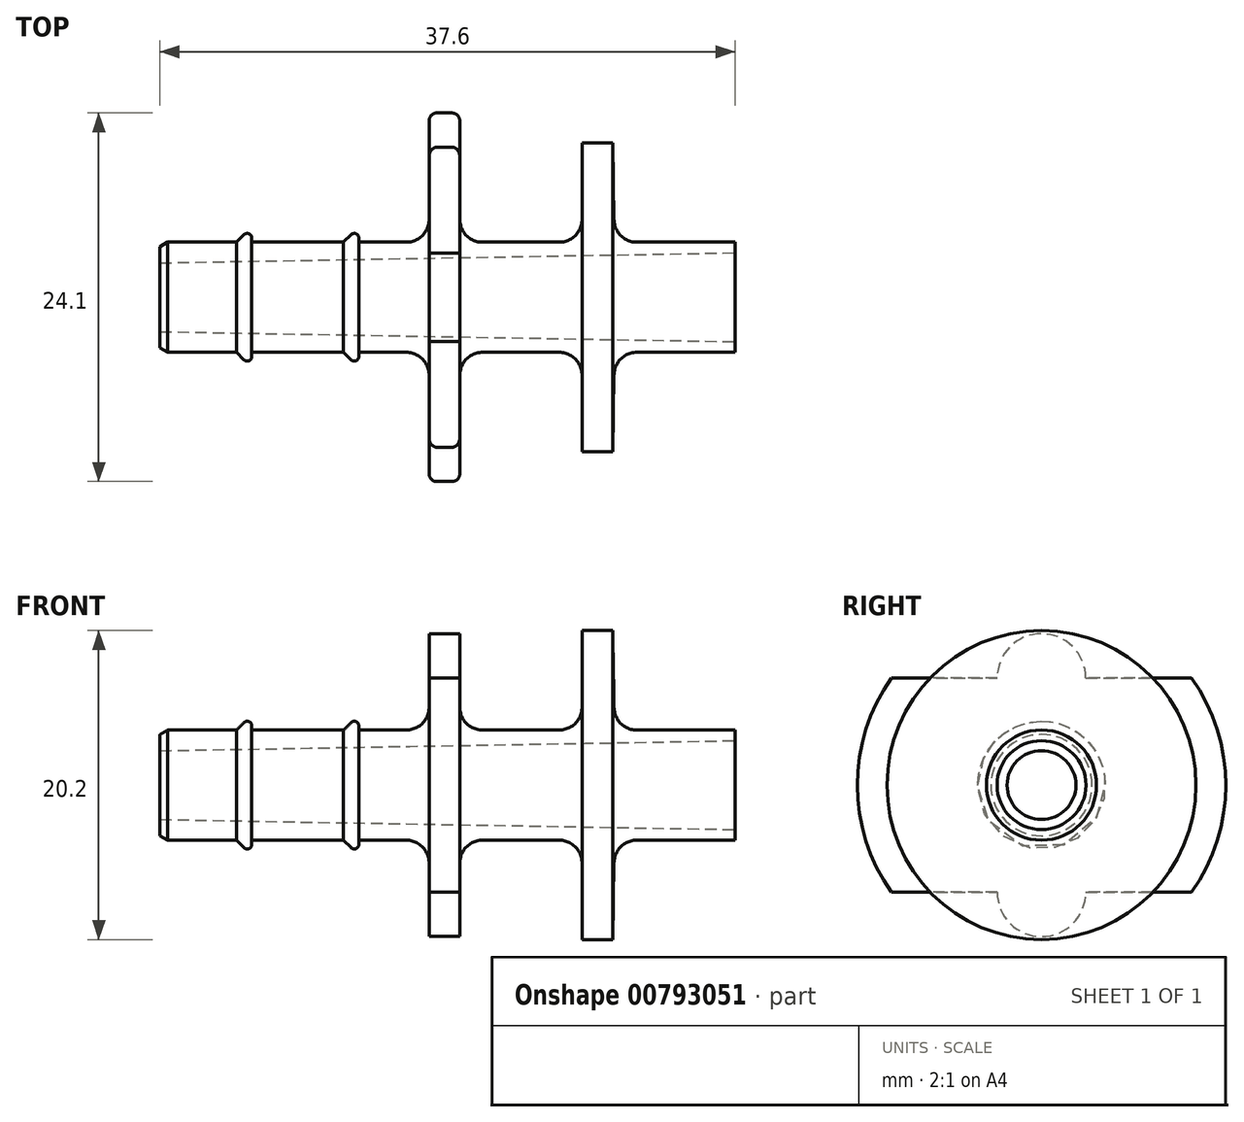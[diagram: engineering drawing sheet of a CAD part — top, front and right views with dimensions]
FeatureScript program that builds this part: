
annotation { "Feature Type Name" : "Feature", "Feature Type Description" : "" }
export const myFeature = defineFeature(function(context is Context, id is Id, definition is map)
    precondition{}
    {
        {
            var Q0;
            Q0=qCreatedBy(makeId("Front.planeOp"),FACE);
            var sketch = newSketch(context, id + "F0", { "sketchPlane" : qUnion([Q0])});
            skLineSegment(sketch, "E0", {"start": v(-19.78, 2.25) * mm, "end": v(17.82, 2.9) * mm});
            skLineSegment(sketch, "E1", {"start": v(17.82, 3.6) * mm, "end": v(11.4, 3.6) * mm});
            skLineSegment(sketch, "E2", {"start": v(17.82, 3.6) * mm, "end": v(17.82, 2.9) * mm});
            skLineSegment(sketch, "E3", {"start": v(-19.78, 3.6) * mm, "end": v(-19.78, 2.25) * mm});
            skLineSegment(sketch, "E4", {"start": v(9.9, 5.07) * mm, "end": v(9.82, 10.1) * mm});
            skLineSegment(sketch, "E5", {"start": v(9.82, 10.1) * mm, "end": v(7.82, 10.1) * mm});
            skLineSegment(sketch, "E6", {"start": v(7.82, 10.1) * mm, "end": v(7.82, 5.1) * mm});
            skLineSegment(sketch, "E7", {"start": v(-0.18, 5.1) * mm, "end": v(-0.18, 11.55) * mm});
            skLineSegment(sketch, "E8", {"start": v(-0.68, 12.05) * mm, "end": v(-1.68, 12.05) * mm});
            skLineSegment(sketch, "E9", {"start": v(-2.18, 11.55) * mm, "end": v(-2.18, 5.1) * mm});
            skLineSegment(sketch, "E10", {"start": v(-9.19, 0) * mm, "end": v(9.2, 0) * mm, "construction": true});
            skPoint(sketch, "E11.visualSharp", {"position": v(-2.18, 12.05) * mm});
            skArc(sketch, "E11.filletArc", {"start": v(-1.68, 12.05) * mm, "mid": v(-2.03, 11.9) * mm, "end": v(-2.18, 11.55) * mm});
            skPoint(sketch, "E12.visualSharp", {"position": v(-0.18, 12.05) * mm});
            skArc(sketch, "E12.filletArc", {"start": v(-0.18, 11.55) * mm, "mid": v(-0.32, 11.9) * mm, "end": v(-0.68, 12.05) * mm});
            skPoint(sketch, "E13.newPointB", {"position": v(-5.55, 3.6) * mm});
            skArc(sketch, "E13.filletArc", {"start": v(9.9, 5.07) * mm, "mid": v(10.36, 4.03) * mm, "end": v(11.4, 3.6) * mm});
            skLineSegment(sketch, "E14", {"start": v(11.4, 3.6) * mm, "end": v(7.82, 3.6) * mm});
            skLineSegment(sketch, "E15", {"start": v(-0.18, 3.6) * mm, "end": v(-2.18, 3.6) * mm});
            skLineSegment(sketch, "E16", {"start": v(1.32, 3.6) * mm, "end": v(6.32, 3.6) * mm});
            skLineSegment(sketch, "E17", {"start": v(-3.68, 3.6) * mm, "end": v(-19.78, 3.6) * mm});
            skPoint(sketch, "E18.visualSharp", {"position": v(7.82, 3.6) * mm});
            skArc(sketch, "E18.filletArc", {"start": v(6.32, 3.6) * mm, "mid": v(7.38, 4.04) * mm, "end": v(7.82, 5.1) * mm});
            skPoint(sketch, "E19.visualSharp", {"position": v(-0.18, 3.6) * mm});
            skArc(sketch, "E19.filletArc", {"start": v(-0.18, 5.1) * mm, "mid": v(0.26, 4.04) * mm, "end": v(1.32, 3.6) * mm});
            skPoint(sketch, "E20.visualSharp", {"position": v(-2.18, 3.6) * mm});
            skArc(sketch, "E20.filletArc", {"start": v(-3.68, 3.6) * mm, "mid": v(-2.62, 4.04) * mm, "end": v(-2.18, 5.1) * mm});
            skLineSegment(sketch, "E21", {"start": v(-19.78, 2.25) * mm, "end": v(14.22, 2.25) * mm, "construction": true});
            skLineSegment(sketch, "E22", {"start": v(-14.78, 3.6) * mm, "end": v(-14.3, 4.09) * mm});
            skLineSegment(sketch, "E23", {"start": v(-13.78, 3.88) * mm, "end": v(-13.78, 3.6) * mm});
            skLineSegment(sketch, "E24", {"start": v(-7.78, 3.6) * mm, "end": v(-7.3, 4.09) * mm});
            skLineSegment(sketch, "E25", {"start": v(-6.78, 3.88) * mm, "end": v(-6.78, 3.6) * mm});
            skPoint(sketch, "E26.visualSharp", {"position": v(-13.78, 4.6) * mm});
            skArc(sketch, "E26.filletArc", {"start": v(-13.78, 3.88) * mm, "mid": v(-13.96, 4.15) * mm, "end": v(-14.3, 4.09) * mm});
            skPoint(sketch, "E27.visualSharp", {"position": v(-6.78, 4.6) * mm});
            skArc(sketch, "E27.filletArc", {"start": v(-6.78, 3.88) * mm, "mid": v(-6.96, 4.15) * mm, "end": v(-7.3, 4.09) * mm});
            skLineSegment(sketch, "E28", {"start": v(-19.78, 3.31) * mm, "end": v(-19.28, 3.6) * mm});
            skSolve(sketch);
        }
        {
            var Q0;
            Q0=makeQuery(id+"F0.imprint","IMPRINT",FACE,{"disambiguationData":[TD([[makeQuery(id+"F0.imprint","IMPRINT",EDGE,{"derivedFrom":sQuery(id+"F0.wireOp",EDGE,"E0")}),1.0]])]});
            var Q1;
            {var subQ0=sQuery(id+"F0.wireOp",EDGE,"E22");Q1=makeQuery(id+"F0.imprint","IMPRINT",FACE,{"disambiguationData":[TD([[makeQuery(id+"F0.imprint","IMPRINT",EDGE,{"derivedFrom":subQ0}),-1.0]])]});}
            var Q2;
            {var subQ0=sQuery(id+"F0.wireOp",EDGE,"E24");Q2=makeQuery(id+"F0.imprint","IMPRINT",FACE,{"disambiguationData":[TD([[makeQuery(id+"F0.imprint","IMPRINT",EDGE,{"derivedFrom":subQ0}),-1.0]])]});}
            var Q3;
            Q3=sQuery(id+"F0.wireOp",EDGE,"E10");
            revolve(context, id + "F1", {"surfaceOperationType" : NewSurfaceOperationType.NEW, "entities" : qUnion([Q0, Q1, Q2]), "axis" : qUnion([Q3]), "revolveType" : RevolveType.FULL});
        }
        {
            var Q0;
            Q0=qCreatedBy(makeId("Right.planeOp"),FACE);
            cPlane(context, id + "F2", {"entities" : qUnion([Q0]), "cplaneType" : CPlaneType.OFFSET, "offset" : 7.9 * mm, "oppositeDirection" : true, "width" : 150 * mm, "height" : 150 * mm});
        }
        {
            var Q0;
            Q0=qCreatedBy(id+"F2.planeOp",FACE);
            var sketch = newSketch(context, id + "F3", { "sketchPlane" : qUnion([Q0])});
            skCircle(sketch, "E29.0", {"center": v(0, 0) * mm, "radius": 12.05 * mm});
            skLineSegment(sketch, "E30", {"start": v(9.8, -7) * mm, "end": v(-9.8, -7) * mm});
            skLineSegment(sketch, "E31", {"start": v(9.8, 7) * mm, "end": v(-9.8, 7) * mm});
            skLineSegment(sketch, "E32", {"start": v(0, 7) * mm, "end": v(0, 12.05) * mm, "construction": true});
            skLineSegment(sketch, "E33", {"start": v(0, -7) * mm, "end": v(0, -12.05) * mm, "construction": true});
            skArc(sketch, "E34", {"start": v(2.9, 7) * mm, "mid": v(0, 9.9) * mm, "end": v(-2.9, 7) * mm});
            skArc(sketch, "E35", {"start": v(-2.9, -7) * mm, "mid": v(0, -9.9) * mm, "end": v(2.9, -7) * mm});
            skSolve(sketch);
        }
        {
            var Q0;
            {var subQ4=sQuery(id+"F3.wireOp",EDGE,"E34");Q0=makeQuery(id+"F3.imprint","IMPRINT",FACE,{"disambiguationData":[TD([[makeQuery(id+"F3.imprint","IMPRINT",EDGE,{"derivedFrom":subQ4}),-1.0]])]});}
            var Q1;
            {var subQ4=sQuery(id+"F3.wireOp",EDGE,"E35");Q1=makeQuery(id+"F3.imprint","IMPRINT",FACE,{"disambiguationData":[TD([[makeQuery(id+"F3.imprint","IMPRINT",EDGE,{"derivedFrom":subQ4}),-1.0]])]});}
            extrude(context, id + "F4", {"entities" : qUnion([Q0, Q1]), "operationType" : NewBodyOperationType.REMOVE, "depth" : 11.1 * mm, "offsetDistance" : 25 * mm});
        }
    });
